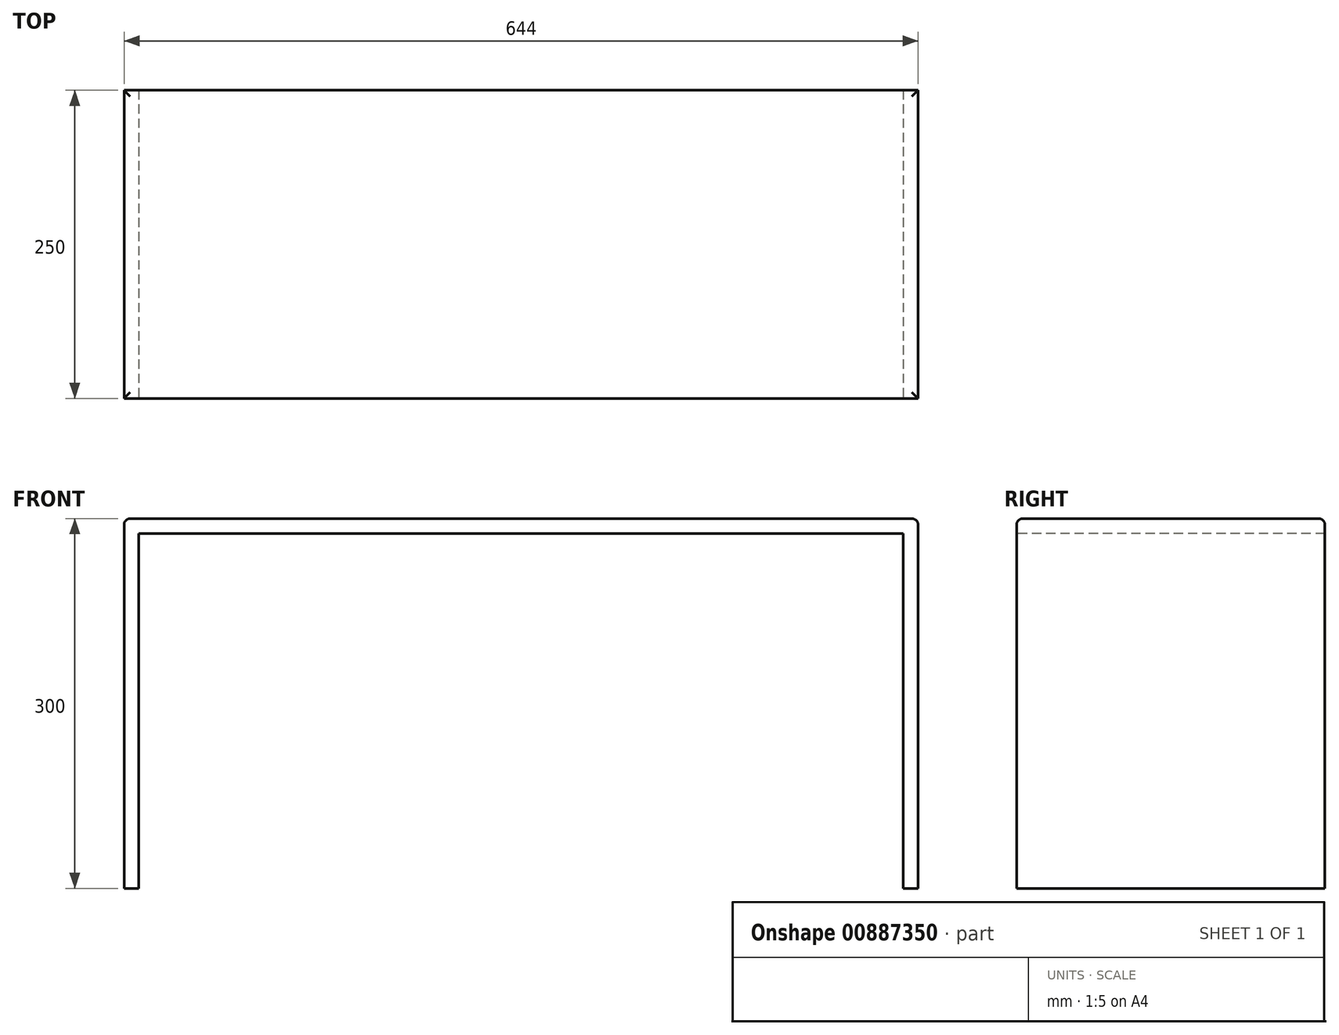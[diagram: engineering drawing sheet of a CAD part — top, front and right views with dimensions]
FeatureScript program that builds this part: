
annotation { "Feature Type Name" : "Feature", "Feature Type Description" : "" }
export const myFeature = defineFeature(function(context is Context, id is Id, definition is map)
    precondition{}
    {
        {
            var Q0;
            Q0=qCreatedBy(makeId("Top.planeOp"),FACE);
            var sketch = newSketch(context, id + "F0", { "sketchPlane" : qUnion([Q0])});
            skLineSegment(sketch, "E0.bottom", {"start": v(0, 0) * mm, "end": v(620, 0) * mm});
            skLineSegment(sketch, "E0.top", {"start": v(0, -250) * mm, "end": v(620, -250) * mm});
            skLineSegment(sketch, "E0.left", {"start": v(0, 0) * mm, "end": v(0, -250) * mm});
            skLineSegment(sketch, "E0.right", {"start": v(620, 0) * mm, "end": v(620, -250) * mm});
            skLineSegment(sketch, "E1", {"start": v(310, 0) * mm, "end": v(310, -250) * mm, "construction": true});
            skSolve(sketch);
        }
        {
            var Q0;
            Q0=makeQuery(id+"F0.imprint","IMPRINT",FACE,{"disambiguationData":[TD([[makeQuery(id+"F0.imprint","IMPRINT",EDGE,{"derivedFrom":sQuery(id+"F0.wireOp",EDGE,"E0.bottom")}),-1.0]])]});
            extrude(context, id + "F1", {"entities" : qUnion([Q0]), "oppositeDirection" : true, "depth" : 12 * mm, "offsetDistance" : 25 * mm});
        }
        {
            var Q0;
            Q0=qCreatedBy(makeId("Top.planeOp"),FACE);
            var sketch = newSketch(context, id + "F2", { "sketchPlane" : qUnion([Q0])});
            skLineSegment(sketch, "E2.bottom", {"start": v(0, 0) * mm, "end": v(-12, 0) * mm});
            skLineSegment(sketch, "E2.top", {"start": v(0, -250) * mm, "end": v(-12, -250) * mm});
            skLineSegment(sketch, "E2.left", {"start": v(0, 0) * mm, "end": v(0, -250) * mm});
            skLineSegment(sketch, "E2.right", {"start": v(-12, 0) * mm, "end": v(-12, -250) * mm});
            skLineSegment(sketch, "E3.0", {"start": v(310, 0) * mm, "end": v(310, -250) * mm, "construction": true});
            skLineSegment(sketch, "E4.MirrorCS", {"start": v(620, 0) * mm, "end": v(632, 0) * mm});
            skLineSegment(sketch, "E5.MirrorCS", {"start": v(632, 0) * mm, "end": v(632, -250) * mm});
            skLineSegment(sketch, "E6.MirrorCS", {"start": v(620, -250) * mm, "end": v(632, -250) * mm});
            skLineSegment(sketch, "E7.MirrorCS", {"start": v(620, 0) * mm, "end": v(620, -250) * mm});
            skSolve(sketch);
        }
        {
            var Q0;
            Q0=makeQuery(id+"F2.imprint","IMPRINT",FACE,{"disambiguationData":[TD([[makeQuery(id+"F2.imprint","IMPRINT",EDGE,{"derivedFrom":sQuery(id+"F2.wireOp",EDGE,"E2.bottom")}),1.0]])]});
            var Q1;
            Q1=makeQuery(id+"F2.imprint","IMPRINT",FACE,{"disambiguationData":[TD([[makeQuery(id+"F2.imprint","IMPRINT",EDGE,{"derivedFrom":sQuery(id+"F2.wireOp",EDGE,"E4.MirrorCS")}),-1.0]])]});
            extrude(context, id + "F3", {"entities" : qUnion([Q0, Q1]), "operationType" : NewBodyOperationType.ADD, "oppositeDirection" : true, "depth" : 300 * mm, "offsetDistance" : 25 * mm});
        }
        {
            var Q0;
            Q0=makeQuery(id+"F3.opExtrude","CAP_EDGE",EDGE,{"disambiguationData":[OSD([sQuery(id+"F2.wireOp",EDGE,"E2.right")])],"isStart":true});
            var Q1;
            Q1=makeQuery(id+"F3.boolean.opBoolean","MERGE",EDGE,{"derivedFrom":[makeQuery(id+"F1.opExtrude","CAP_EDGE",EDGE,{"disambiguationData":[OSD([sQuery(id+"F0.wireOp",EDGE,"E0.top")])],"isStart":true}),makeQuery(id+"F3.opExtrude","CAP_EDGE",EDGE,{"disambiguationData":[OSD([sQuery(id+"F2.wireOp",EDGE,"E2.top")])],"isStart":true}),makeQuery(id+"F3.opExtrude","CAP_EDGE",EDGE,{"disambiguationData":[OSD([sQuery(id+"F2.wireOp",EDGE,"E6.MirrorCS")])],"isStart":true})]});
            var Q2;
            Q2=makeQuery(id+"F3.opExtrude","CAP_EDGE",EDGE,{"disambiguationData":[OSD([sQuery(id+"F2.wireOp",EDGE,"E5.MirrorCS")])],"isStart":true});
            var Q3;
            Q3=makeQuery(id+"F3.boolean.opBoolean","MERGE",EDGE,{"derivedFrom":[makeQuery(id+"F1.opExtrude","CAP_EDGE",EDGE,{"disambiguationData":[OSD([sQuery(id+"F0.wireOp",EDGE,"E0.bottom")])],"isStart":true}),makeQuery(id+"F3.opExtrude","CAP_EDGE",EDGE,{"disambiguationData":[OSD([sQuery(id+"F2.wireOp",EDGE,"E2.bottom")])],"isStart":true}),makeQuery(id+"F3.opExtrude","CAP_EDGE",EDGE,{"disambiguationData":[OSD([sQuery(id+"F2.wireOp",EDGE,"E4.MirrorCS")])],"isStart":true})]});
            fillet(context, id + "F4", {"entities" : qUnion([Q0, Q1, Q2, Q3]), "radius" : 5 * mm, "tangentPropagation" : true, "allowEdgeOverflow" : false});
        }
    });
